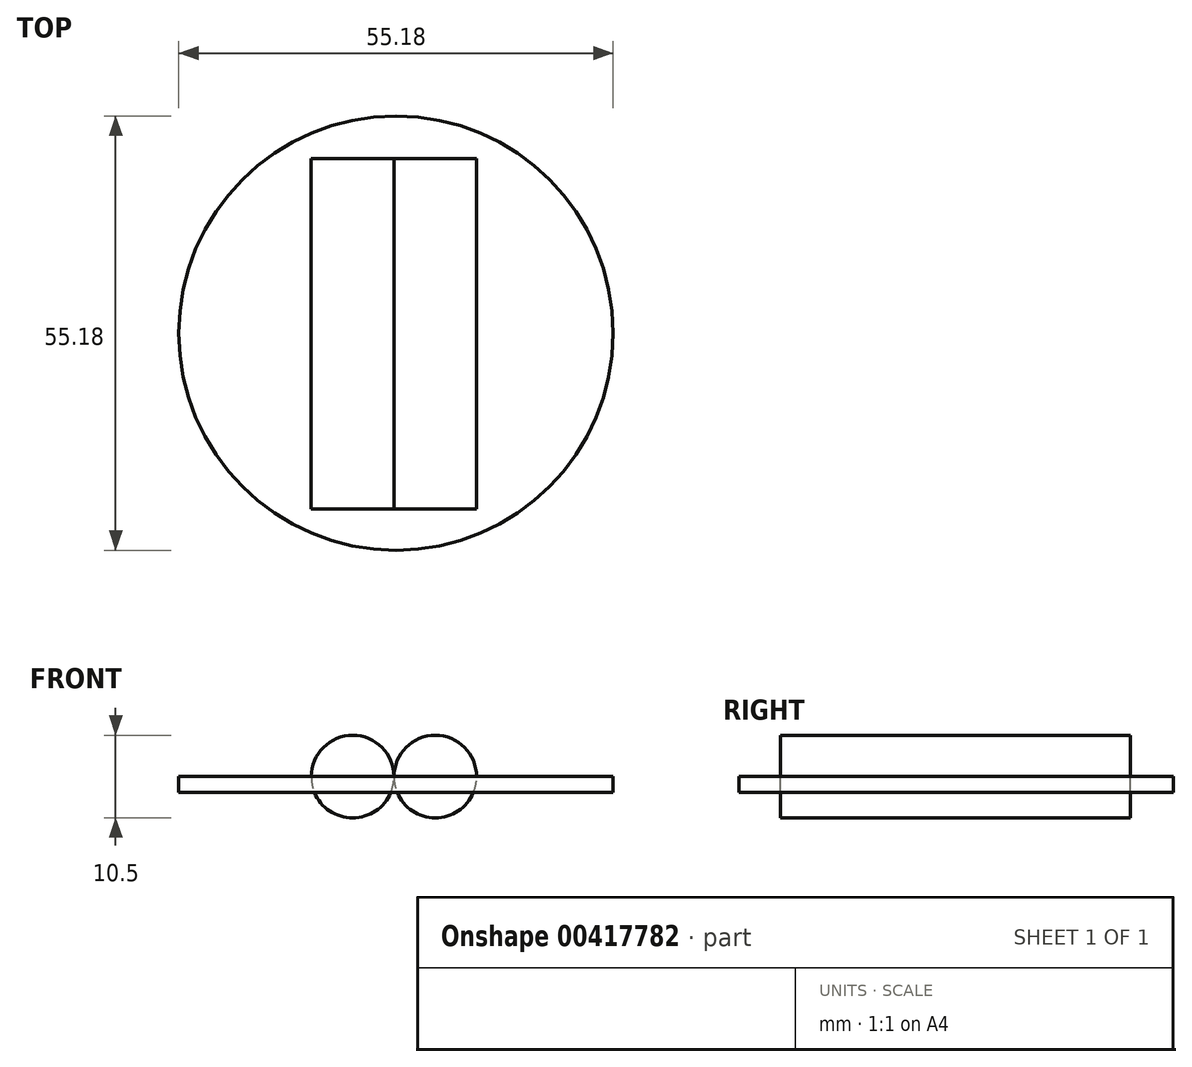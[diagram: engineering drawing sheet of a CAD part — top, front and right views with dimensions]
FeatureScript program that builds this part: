
annotation { "Feature Type Name" : "Feature", "Feature Type Description" : "" }
export const myFeature = defineFeature(function(context is Context, id is Id, definition is map)
    precondition{}
    {
        {
            var Q0;
            Q0=qCreatedBy(makeId("Front.planeOp"),FACE);
            var sketch = newSketch(context, id + "F0", { "sketchPlane" : qUnion([Q0])});
            skCircle(sketch, "E0", {"center": v(-7.62, 0) * mm, "radius": 5.25 * mm});
            skCircle(sketch, "E1", {"center": v(2.88, 0) * mm, "radius": 5.25 * mm});
            skSolve(sketch);
        }
        {
            var Q0;
            Q0 = qSketchRegion(id + "F0", true);
            extrude(context, id + "F1", {"entities" : qUnion([Q0]), "depth" : 44.5 * mm});
        }
        {
            var Q0;
            Q0=qCreatedBy(makeId("Top.planeOp"),FACE);
            var sketch = newSketch(context, id + "F2", { "sketchPlane" : qUnion([Q0])});
            skCircle(sketch, "E2", {"center": v(-2.12, -22.15) * mm, "radius": 27.59 * mm});
            skSolve(sketch);
        }
        {
            var Q0;
            Q0 = qSketchRegion(id + "F2", true);
            extrude(context, id + "F3", {"entities" : qUnion([Q0]), "depth" : 0 * mm, "hasSecondDirection" : true, "secondDirectionOppositeDirection" : true, "secondDirectionDepth" : 2 * mm});
        }
    });
